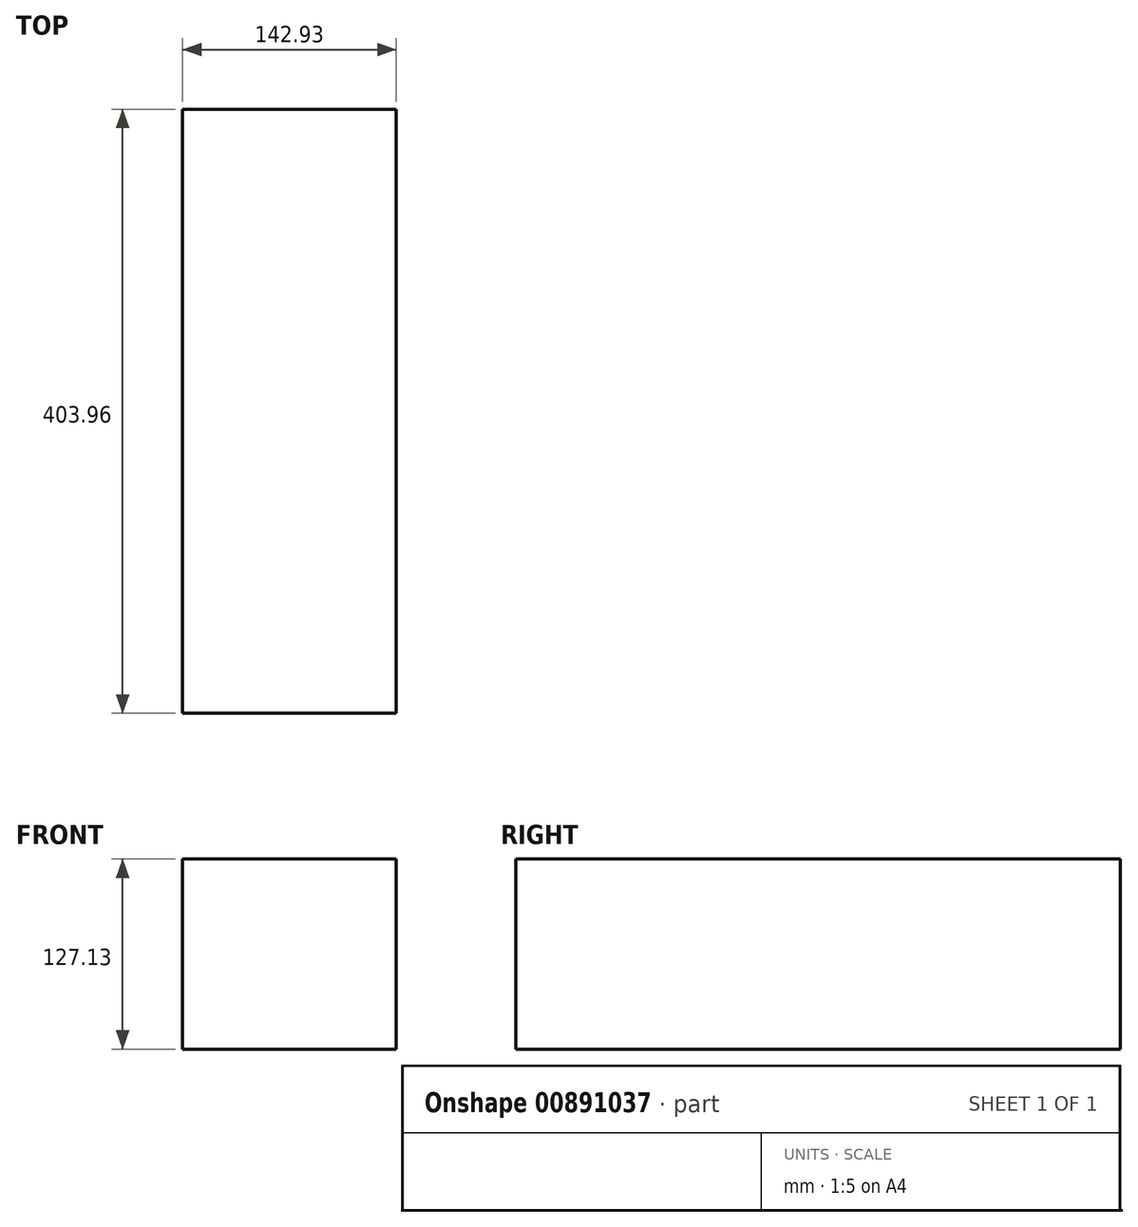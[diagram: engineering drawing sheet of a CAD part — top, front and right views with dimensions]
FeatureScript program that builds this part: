
annotation { "Feature Type Name" : "Feature", "Feature Type Description" : "" }
export const myFeature = defineFeature(function(context is Context, id is Id, definition is map)
    precondition{}
    {
        {
            var Q0;
            Q0=qCreatedBy(makeId("Front.planeOp"),FACE);
            var sketch = newSketch(context, id + "F0", { "sketchPlane" : qUnion([Q0])});
            skLineSegment(sketch, "E0.bottom", {"start": v(-72.04, 55.91) * mm, "end": v(70.9, 55.91) * mm});
            skLineSegment(sketch, "E0.top", {"start": v(-72.04, -71.22) * mm, "end": v(70.9, -71.22) * mm});
            skLineSegment(sketch, "E0.left", {"start": v(-72.04, 55.91) * mm, "end": v(-72.04, -71.22) * mm});
            skLineSegment(sketch, "E0.right", {"start": v(70.9, 55.91) * mm, "end": v(70.9, -71.22) * mm});
            skSolve(sketch);
        }
        {
            var Q0;
            Q0=makeQuery(id+"F0.imprint","IMPRINT",FACE,{"disambiguationData":[TD([[makeQuery(id+"F0.imprint","IMPRINT",EDGE,{"derivedFrom":sQuery(id+"F0.wireOp",EDGE,"E0.bottom")}),-1.0]])]});
            extrude(context, id + "F1", {"entities" : qUnion([Q0]), "depth" : 403.96 * mm, "offsetDistance" : 25.4 * mm});
        }
    });
